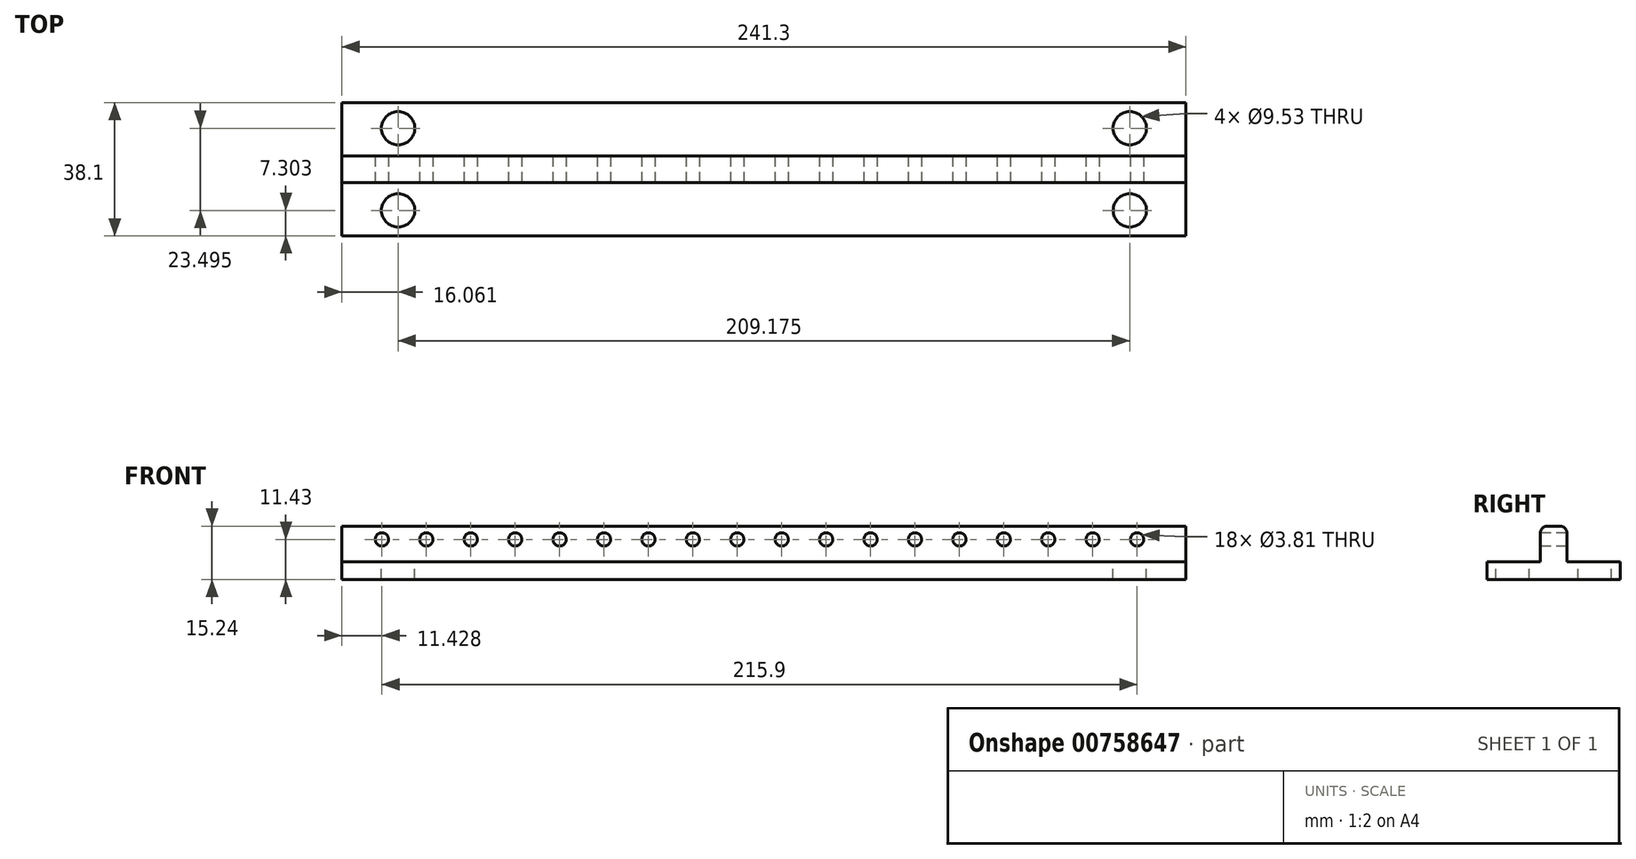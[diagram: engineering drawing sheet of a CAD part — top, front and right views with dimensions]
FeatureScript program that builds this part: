
annotation { "Feature Type Name" : "Feature", "Feature Type Description" : "" }
export const myFeature = defineFeature(function(context is Context, id is Id, definition is map)
    precondition{}
    {
        {
            var Q0;
            Q0=qCreatedBy(makeId("Top.planeOp"),FACE);
            var sketch = newSketch(context, id + "F0", { "sketchPlane" : qUnion([Q0])});
            skLineSegment(sketch, "E0.bottom", {"start": v(-130.78, 0) * mm, "end": v(110.52, 0) * mm});
            skLineSegment(sketch, "E0.top", {"start": v(-130.78, 38.1) * mm, "end": v(110.52, 38.1) * mm});
            skLineSegment(sketch, "E0.left", {"start": v(-130.78, 0) * mm, "end": v(-130.78, 38.1) * mm});
            skLineSegment(sketch, "E0.right", {"start": v(110.52, 0) * mm, "end": v(110.52, 38.1) * mm});
            skSolve(sketch);
        }
        {
            var Q0;
            Q0 = qSketchRegion(id + "F0", true);
            extrude(context, id + "F1", {"entities" : qUnion([Q0]), "depth" : 5.08 * mm, "offsetDistance" : 25.4 * mm});
        }
        {
            var Q0;
            Q0=makeQuery(id+"F1.opExtrude","CAP_FACE",FACE,{"disambiguationData":[OSD([sQuery(id+"F0.wireOp",EDGE,"E0.bottom"),sQuery(id+"F0.wireOp",EDGE,"E0.top"),sQuery(id+"F0.wireOp",EDGE,"E0.left"),sQuery(id+"F0.wireOp",EDGE,"E0.right")])],"isStart":false});
            var sketch = newSketch(context, id + "F2", { "sketchPlane" : qUnion([Q0])});
            skLineSegment(sketch, "E1.bottom", {"start": v(-130.78, 22.86) * mm, "end": v(110.52, 22.86) * mm});
            skLineSegment(sketch, "E1.top", {"start": v(-130.78, 15.24) * mm, "end": v(110.52, 15.24) * mm});
            skLineSegment(sketch, "E1.left", {"start": v(-130.78, 22.86) * mm, "end": v(-130.78, 15.24) * mm});
            skLineSegment(sketch, "E1.right", {"start": v(110.52, 22.86) * mm, "end": v(110.52, 15.24) * mm});
            skSolve(sketch);
        }
        {
            var Q0;
            Q0 = qSketchRegion(id + "F2", true);
            extrude(context, id + "F3", {"entities" : qUnion([Q0]), "operationType" : NewBodyOperationType.ADD, "depth" : 10.16 * mm, "offsetDistance" : 25.4 * mm});
        }
        {
            var Q0;
            Q0=makeQuery(id+"F3.opExtrude","SWEPT_FACE",FACE,{"disambiguationData":[OSD([sQuery(id+"F2.wireOp",EDGE,"E1.top")])]});
            var sketch = newSketch(context, id + "F4", { "sketchPlane" : qUnion([Q0])});
            skCircle(sketch, "E2", {"center": v(-119.35, 11.43) * mm, "radius": 1.9 * mm});
            skCircle(sketch, "E3.1.0.0", {"center": v(-106.65, 11.43) * mm, "radius": 1.9 * mm});
            skCircle(sketch, "E3.2.0.0", {"center": v(-93.95, 11.43) * mm, "radius": 1.9 * mm});
            skCircle(sketch, "E3.3.0.0", {"center": v(-81.25, 11.43) * mm, "radius": 1.9 * mm});
            skCircle(sketch, "E3.4.0.0", {"center": v(-68.55, 11.43) * mm, "radius": 1.9 * mm});
            skCircle(sketch, "E3.5.0.0", {"center": v(-55.85, 11.43) * mm, "radius": 1.9 * mm});
            skCircle(sketch, "E3.6.0.0", {"center": v(-43.15, 11.43) * mm, "radius": 1.9 * mm});
            skCircle(sketch, "E3.7.0.0", {"center": v(-30.45, 11.43) * mm, "radius": 1.9 * mm});
            skCircle(sketch, "E3.8.0.0", {"center": v(-17.75, 11.43) * mm, "radius": 1.9 * mm});
            skCircle(sketch, "E3.9.0.0", {"center": v(-5.05, 11.43) * mm, "radius": 1.9 * mm});
            skCircle(sketch, "E3.10.0.0", {"center": v(7.65, 11.43) * mm, "radius": 1.9 * mm});
            skCircle(sketch, "E3.11.0.0", {"center": v(20.35, 11.43) * mm, "radius": 1.9 * mm});
            skLineSegment(sketch, "E3.direction1", {"start": v(-119.35, 11.43) * mm, "end": v(-106.65, 11.43) * mm, "construction": true});
            skCircle(sketch, "E4.0.12.0", {"center": v(33.05, 11.43) * mm, "radius": 1.9 * mm});
            skCircle(sketch, "E4.0.13.0", {"center": v(45.75, 11.43) * mm, "radius": 1.9 * mm});
            skCircle(sketch, "E4.0.14.0", {"center": v(58.45, 11.43) * mm, "radius": 1.9 * mm});
            skCircle(sketch, "E4.0.15.0", {"center": v(71.15, 11.43) * mm, "radius": 1.9 * mm});
            skCircle(sketch, "E4.0.16.0", {"center": v(83.85, 11.43) * mm, "radius": 1.9 * mm});
            skCircle(sketch, "E5.0.17.0", {"center": v(96.55, 11.43) * mm, "radius": 1.9 * mm});
            skSolve(sketch);
        }
        {
            var Q0;
            Q0 = qSketchRegion(id + "F4", true);
            extrude(context, id + "F5", {"entities" : qUnion([Q0]), "operationType" : NewBodyOperationType.REMOVE, "endBound" : BoundingType.THROUGH_ALL, "oppositeDirection" : true, "depth" : 25.4 * mm, "offsetDistance" : 25.4 * mm});
        }
        {
            var Q0;
            {var subQ0=sQuery(id+"F0.wireOp",EDGE,"E0.right");var subQ1=sQuery(id+"F0.wireOp",EDGE,"E0.left");var subQ2=sQuery(id+"F0.wireOp",EDGE,"E0.top");Q0=makeQuery(id+"F3.boolean.opBoolean","SPLIT",FACE,{"disambiguationData":[TD([makeQuery(id+"F1.opExtrude","SWEPT_FACE",FACE,{"disambiguationData":[OSD([subQ2])]})])],"derivedFrom":makeQuery(id+"F1.opExtrude","CAP_FACE",FACE,{"disambiguationData":[OSD([sQuery(id+"F0.wireOp",EDGE,"E0.bottom"),subQ2,subQ1,subQ0])],"isStart":false})});}
            var sketch = newSketch(context, id + "F6", { "sketchPlane" : qUnion([Q0])});
            skCircle(sketch, "E6", {"center": v(-114.72, 30.8) * mm, "radius": 4.76 * mm});
            skCircle(sketch, "E7", {"center": v(94.45, 30.8) * mm, "radius": 4.76 * mm});
            skSolve(sketch);
        }
        {
            var Q0;
            {var subQ0=sQuery(id+"F0.wireOp",EDGE,"E0.left");var subQ1=sQuery(id+"F0.wireOp",EDGE,"E0.right");var subQ2=sQuery(id+"F0.wireOp",EDGE,"E0.bottom");Q0=makeQuery(id+"F3.boolean.opBoolean","SPLIT",FACE,{"disambiguationData":[TD([makeQuery(id+"F1.opExtrude","SWEPT_FACE",FACE,{"disambiguationData":[OSD([subQ2])]})])],"derivedFrom":makeQuery(id+"F1.opExtrude","CAP_FACE",FACE,{"disambiguationData":[OSD([subQ2,sQuery(id+"F0.wireOp",EDGE,"E0.top"),subQ0,subQ1])],"isStart":false})});}
            var sketch = newSketch(context, id + "F7", { "sketchPlane" : qUnion([Q0])});
            skCircle(sketch, "E8", {"center": v(94.46, 7.3) * mm, "radius": 4.76 * mm});
            skCircle(sketch, "E9", {"center": v(-114.72, 7.3) * mm, "radius": 4.76 * mm});
            skSolve(sketch);
        }
        {
            var Q0;
            Q0=makeQuery(id+"F6.imprint","IMPRINT",FACE,{"disambiguationData":[TD([[makeQuery(id+"F6.imprint","IMPRINT",EDGE,{"derivedFrom":sQuery(id+"F6.wireOp",EDGE,"E6")}),1.0]])]});
            var Q1;
            Q1=makeQuery(id+"F7.imprint","IMPRINT",FACE,{"disambiguationData":[TD([[makeQuery(id+"F7.imprint","IMPRINT",EDGE,{"derivedFrom":sQuery(id+"F7.wireOp",EDGE,"E9")}),1.0]])]});
            var Q2;
            Q2=makeQuery(id+"F6.imprint","IMPRINT",FACE,{"disambiguationData":[TD([[makeQuery(id+"F6.imprint","IMPRINT",EDGE,{"derivedFrom":sQuery(id+"F6.wireOp",EDGE,"E7")}),1.0]])]});
            var Q3;
            Q3=makeQuery(id+"F7.imprint","IMPRINT",FACE,{"disambiguationData":[TD([[makeQuery(id+"F7.imprint","IMPRINT",EDGE,{"derivedFrom":sQuery(id+"F7.wireOp",EDGE,"E8")}),1.0]])]});
            extrude(context, id + "F8", {"entities" : qUnion([Q0, Q1, Q2, Q3]), "operationType" : NewBodyOperationType.REMOVE, "endBound" : BoundingType.THROUGH_ALL, "oppositeDirection" : true, "depth" : 25.4 * mm, "offsetDistance" : 25.4 * mm});
        }
        {
            var Q0;
            Q0=makeQuery(id+"F3.opExtrude","CAP_EDGE",EDGE,{"disambiguationData":[OSD([sQuery(id+"F2.wireOp",EDGE,"E1.top")])],"isStart":false});
            var Q1;
            Q1=makeQuery(id+"F3.opExtrude","CAP_EDGE",EDGE,{"disambiguationData":[OSD([sQuery(id+"F2.wireOp",EDGE,"E1.bottom")])],"isStart":false});
            fillet(context, id + "F9", {"entities" : qUnion([Q0, Q1]), "radius" : 2.03 * mm, "tangentPropagation" : true, "allowEdgeOverflow" : false});
        }
    });
